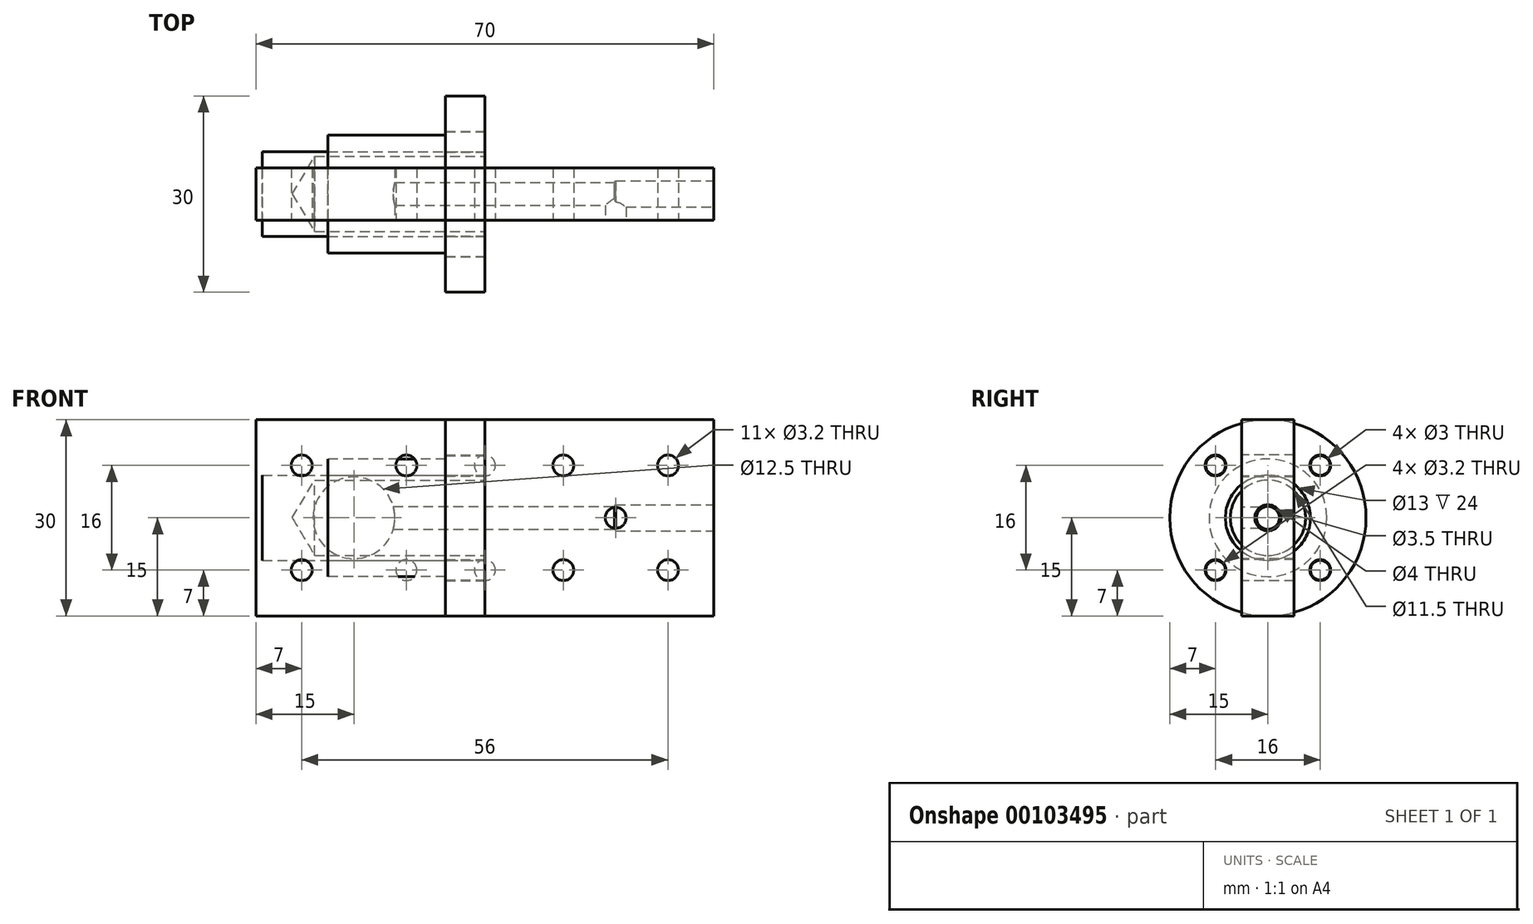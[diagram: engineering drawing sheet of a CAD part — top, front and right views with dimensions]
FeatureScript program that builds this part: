
annotation { "Feature Type Name" : "Feature", "Feature Type Description" : "" }
export const myFeature = defineFeature(function(context is Context, id is Id, definition is map)
    precondition{}
    {
        {
            var Q0;
            Q0=qCreatedBy(makeId("Front.planeOp"),FACE);
            var sketch = newSketch(context, id + "F0", { "sketchPlane" : qUnion([Q0])});
            skLineSegment(sketch, "E0.bottom", {"start": v(35, -15) * mm, "end": v(-35, -15) * mm});
            skLineSegment(sketch, "E0.top", {"start": v(35, 15) * mm, "end": v(-35, 15) * mm});
            skLineSegment(sketch, "E0.left", {"start": v(35, -15) * mm, "end": v(35, 15) * mm});
            skLineSegment(sketch, "E0.right", {"start": v(-35, -15) * mm, "end": v(-35, 15) * mm});
            skPoint(sketch, "E0.middle", {"position": v(0, 0) * mm});
            skSolve(sketch);
        }
        {
            var Q0;
            Q0=makeQuery(id+"F0.imprint","IMPRINT",FACE,{"disambiguationData":[TD([[makeQuery(id+"F0.imprint","IMPRINT",EDGE,{"derivedFrom":sQuery(id+"F0.wireOp",EDGE,"E0.bottom")}),-1.0]])]});
            extrude(context, id + "F1", {"entities" : qUnion([Q0]), "endBound" : BoundingType.SYMMETRIC, "depth" : 8 * mm});
        }
        {
            var Q0;
            Q0=makeQuery(id+"F1.opExtrude","CAP_FACE",FACE,{"disambiguationData":[OSD([sQuery(id+"F0.wireOp",EDGE,"E0.bottom"),sQuery(id+"F0.wireOp",EDGE,"E0.top"),sQuery(id+"F0.wireOp",EDGE,"E0.left"),sQuery(id+"F0.wireOp",EDGE,"E0.right")])],"isStart":false});
            var sketch = newSketch(context, id + "F2", { "sketchPlane" : qUnion([Q0])});
            skCircle(sketch, "E1", {"center": v(-20, 0) * mm, "radius": 6.25 * mm});
            skCircle(sketch, "E2", {"center": v(-28, 8) * mm, "radius": 1.6 * mm});
            skCircle(sketch, "E3", {"center": v(-12, 8) * mm, "radius": 1.6 * mm});
            skCircle(sketch, "E4", {"center": v(12, 8) * mm, "radius": 1.6 * mm});
            skCircle(sketch, "E5", {"center": v(28, 8) * mm, "radius": 1.6 * mm});
            skCircle(sketch, "E6", {"center": v(28, -8) * mm, "radius": 1.6 * mm});
            skCircle(sketch, "E7", {"center": v(12, -8) * mm, "radius": 1.6 * mm});
            skCircle(sketch, "E8", {"center": v(-12, -8) * mm, "radius": 1.6 * mm});
            skCircle(sketch, "E9", {"center": v(-28, -8) * mm, "radius": 1.6 * mm});
            skCircle(sketch, "E10", {"center": v(0, 8) * mm, "radius": 1.6 * mm});
            skCircle(sketch, "E11", {"center": v(0, -8) * mm, "radius": 1.6 * mm});
            skSolve(sketch);
        }
        {
            var Q0;
            Q0 = qSketchRegion(id + "F2", true);
            extrude(context, id + "F3", {"entities" : qUnion([Q0]), "operationType" : NewBodyOperationType.REMOVE, "endBound" : BoundingType.THROUGH_ALL, "oppositeDirection" : true, "depth" : 25 * mm});
        }
        {
            var Q0;
            Q0=makeQuery(id+"F1.opExtrude","CAP_FACE",FACE,{"disambiguationData":[OSD([sQuery(id+"F0.wireOp",EDGE,"E0.bottom"),sQuery(id+"F0.wireOp",EDGE,"E0.top"),sQuery(id+"F0.wireOp",EDGE,"E0.left"),sQuery(id+"F0.wireOp",EDGE,"E0.right")])],"isStart":false});
            var sketch = newSketch(context, id + "F4", { "sketchPlane" : qUnion([Q0])});
            skCircle(sketch, "E12", {"center": v(20, 0) * mm, "radius": 1.6 * mm});
            skPoint(sketch, "E12.centerSnap0", {"position": v(35, 0) * mm});
            skSolve(sketch);
        }
        {
            var Q0;
            Q0 = qSketchRegion(id + "F4", true);
            extrude(context, id + "F5", {"entities" : qUnion([Q0]), "operationType" : NewBodyOperationType.REMOVE, "oppositeDirection" : true, "depth" : 4 * mm});
        }
        {
            var Q0;
            Q0=makeQuery(id+"F1.opExtrude","SWEPT_FACE",FACE,{"disambiguationData":[OSD([sQuery(id+"F0.wireOp",EDGE,"E0.left")])]});
            var sketch = newSketch(context, id + "F6", { "sketchPlane" : qUnion([Q0])});
            skCircle(sketch, "E13", {"center": v(0, 0) * mm, "radius": 1.75 * mm});
            skSolve(sketch);
        }
        {
            var Q0;
            Q0 = qSketchRegion(id + "F6", true);
            var Q1;
            Q1=makeQuery(id+"F3.boolean.opBoolean","COPY",FACE,{"derivedFrom":makeQuery(id+"F3.opExtrude","SWEPT_FACE",FACE,{"disambiguationData":[OSD([sQuery(id+"F2.wireOp",EDGE,"E1")])]})});
            extrude(context, id + "F7", {"entities" : qUnion([Q0]), "operationType" : NewBodyOperationType.REMOVE, "endBound" : BoundingType.UP_TO_SURFACE, "oppositeDirection" : true, "endBoundEntityFace" : qUnion([Q1]), "depth" : 50 * mm});
        }
        {
            var Q0;
            Q0=makeQuery(id+"F1.opExtrude","SWEPT_FACE",FACE,{"disambiguationData":[OSD([sQuery(id+"F0.wireOp",EDGE,"E0.left")])]});
            var sketch = newSketch(context, id + "F8", { "sketchPlane" : qUnion([Q0])});
            skCircle(sketch, "E14", {"center": v(0, 0) * mm, "radius": 2 * mm});
            skSolve(sketch);
        }
        {
            var Q0;
            Q0=qCreatedBy(makeId("Front.planeOp"),FACE);
            var sketch = newSketch(context, id + "F9", { "sketchPlane" : qUnion([Q0])});
            skLineSegment(sketch, "E15", {"start": v(-24, 0) * mm, "end": v(-24, 9) * mm});
            skLineSegment(sketch, "E16", {"start": v(-24, 9) * mm, "end": v(-6, 9) * mm});
            skLineSegment(sketch, "E17", {"start": v(-6, 9) * mm, "end": v(-6, 15) * mm});
            skLineSegment(sketch, "E18", {"start": v(-6, 15) * mm, "end": v(0, 15) * mm});
            skLineSegment(sketch, "E19", {"start": v(0, 15) * mm, "end": v(0, 0) * mm});
            skLineSegment(sketch, "E20", {"start": v(-24, 0) * mm, "end": v(0, 0) * mm});
            skSolve(sketch);
        }
        {
            var Q0;
            Q0=makeQuery(id+"F9.imprint","IMPRINT",FACE,{"disambiguationData":[TD([[makeQuery(id+"F9.imprint","IMPRINT",EDGE,{"derivedFrom":sQuery(id+"F9.wireOp",EDGE,"E15")}),-1.0]])]});
            var Q1;
            Q1=sQuery(id+"F9.wireOp",EDGE,"E20");
            revolve(context, id + "F10", {"entities" : qUnion([Q0]), "axis" : qUnion([Q1]), "revolveType" : RevolveType.FULL});
        }
        {
            var Q0;
            Q0=makeQuery(id+"F10.opRevolve","SWEPT_FACE",FACE,{"disambiguationData":[OSD([sQuery(id+"F9.wireOp",EDGE,"E19")])]});
            var sketch = newSketch(context, id + "F11", { "sketchPlane" : qUnion([Q0])});
            skPoint(sketch, "E21", {"position": v(0, 0) * mm});
            skPoint(sketch, "E22", {"position": v(-8, 8) * mm});
            skPoint(sketch, "E23.MirrorP", {"position": v(8, 8) * mm});
            skPoint(sketch, "E24.MirrorP", {"position": v(-8, -8) * mm});
            skPoint(sketch, "E25.MirrorP", {"position": v(8, -8) * mm});
            skSolve(sketch);
        }
        {
            var Q0;
            Q0=sQuery(id+"F11.wireOp",VERTEX,"E22");
            var Q1;
            Q1=sQuery(id+"F11.wireOp",VERTEX,"E23.MirrorP");
            var Q2;
            Q2=sQuery(id+"F11.wireOp",VERTEX,"E25.MirrorP");
            var Q3;
            Q3=sQuery(id+"F11.wireOp",VERTEX,"E24.MirrorP");
            var Q4;
            Q4=makeQuery(id+"F10.opRevolve","SWEPT_BODY",BODY,{"disambiguationData":[OSD([sQuery(id+"F9.wireOp",EDGE,"E15"),sQuery(id+"F9.wireOp",EDGE,"E16"),sQuery(id+"F9.wireOp",EDGE,"E17"),sQuery(id+"F9.wireOp",EDGE,"E18"),sQuery(id+"F9.wireOp",EDGE,"E19"),sQuery(id+"F9.wireOp",EDGE,"E20")])]});
            hole(context, id + "F12", {"style" : HoleStyle.SIMPLE, "endStyle" : HoleEndStyle.THROUGH, "holeDiameter" : 3 * mm, "locations" : qUnion([Q0, Q1, Q2, Q3]), "scope" : qUnion([Q4]), "isTappedThrough" : true});
        }
        {
            var Q0;
            Q0=sQuery(id+"F11.wireOp",VERTEX,"E21");
            var Q1;
            Q1=makeQuery(id+"F10.opRevolve","SWEPT_BODY",BODY,{"disambiguationData":[OSD([sQuery(id+"F9.wireOp",EDGE,"E15"),sQuery(id+"F9.wireOp",EDGE,"E16"),sQuery(id+"F9.wireOp",EDGE,"E17"),sQuery(id+"F9.wireOp",EDGE,"E18"),sQuery(id+"F9.wireOp",EDGE,"E19"),sQuery(id+"F9.wireOp",EDGE,"E20")])]});
            hole(context, id + "F13", {"style" : HoleStyle.SIMPLE, "endStyle" : HoleEndStyle.THROUGH, "holeDiameter" : 13 * mm, "locations" : qUnion([Q0]), "scope" : qUnion([Q1]), "isTappedThrough" : true});
        }
        {
            var Q0;
            Q0=sQuery(id+"F8.wireOp",VERTEX,"E14.center");
            var Q1;
            Q1=makeQuery(id+"F1.opExtrude","SWEPT_BODY",BODY,{"disambiguationData":[OSD([sQuery(id+"F0.wireOp",EDGE,"E0.bottom"),sQuery(id+"F0.wireOp",EDGE,"E0.top"),sQuery(id+"F0.wireOp",EDGE,"E0.left"),sQuery(id+"F0.wireOp",EDGE,"E0.right")])]});
            hole(context, id + "F14", {"style" : HoleStyle.SIMPLE, "endStyle" : HoleEndStyle.BLIND, "holeDiameter" : 4 * mm, "holeDepth" : 15 * mm, "locations" : qUnion([Q0]), "scope" : qUnion([Q1])});
        }
        {
            var Q0;
            Q0=qCreatedBy(makeId("Front.planeOp"),FACE);
            var sketch = newSketch(context, id + "F15", { "sketchPlane" : qUnion([Q0])});
            skLineSegment(sketch, "E26", {"start": v(0, 0) * mm, "end": v(-34, 0) * mm});
            skLineSegment(sketch, "E27", {"start": v(-34, 0) * mm, "end": v(-34, 6.5) * mm});
            skLineSegment(sketch, "E28", {"start": v(-34, 6.5) * mm, "end": v(-6, 6.5) * mm});
            skLineSegment(sketch, "E29", {"start": v(-6, 6.5) * mm, "end": v(-6, 15) * mm});
            skLineSegment(sketch, "E30", {"start": v(-6, 15) * mm, "end": v(0, 15) * mm});
            skLineSegment(sketch, "E31", {"start": v(0, 15) * mm, "end": v(0, 0) * mm});
            skSolve(sketch);
        }
        {
            var Q0;
            Q0=makeQuery(id+"F15.imprint","IMPRINT",FACE,{"disambiguationData":[TD([[makeQuery(id+"F15.imprint","IMPRINT",EDGE,{"derivedFrom":sQuery(id+"F15.wireOp",EDGE,"E26")}),-1.0]])]});
            var Q1;
            Q1=sQuery(id+"F15.wireOp",EDGE,"E26");
            revolve(context, id + "F16", {"entities" : qUnion([Q0]), "axis" : qUnion([Q1]), "revolveType" : RevolveType.FULL});
        }
        {
            var Q0;
            Q0=sQuery(id+"F11.wireOp",VERTEX,"E22");
            var Q1;
            Q1=sQuery(id+"F11.wireOp",VERTEX,"E23.MirrorP");
            var Q2;
            Q2=sQuery(id+"F11.wireOp",VERTEX,"E25.MirrorP");
            var Q3;
            Q3=sQuery(id+"F11.wireOp",VERTEX,"E24.MirrorP");
            var Q4;
            Q4=makeQuery(id+"F16.opRevolve","SWEPT_BODY",BODY,{"disambiguationData":[OSD([sQuery(id+"F15.wireOp",EDGE,"E26"),sQuery(id+"F15.wireOp",EDGE,"E27"),sQuery(id+"F15.wireOp",EDGE,"E28"),sQuery(id+"F15.wireOp",EDGE,"E29"),sQuery(id+"F15.wireOp",EDGE,"E30"),sQuery(id+"F15.wireOp",EDGE,"E31")])]});
            hole(context, id + "F17", {"style" : HoleStyle.SIMPLE, "endStyle" : HoleEndStyle.THROUGH, "holeDiameter" : 3.2 * mm, "locations" : qUnion([Q0, Q1, Q2, Q3]), "scope" : qUnion([Q4]), "isTappedThrough" : true});
        }
        {
            var Q0;
            Q0=sQuery(id+"F11.wireOp",VERTEX,"E21");
            var Q1;
            Q1=makeQuery(id+"F16.opRevolve","SWEPT_BODY",BODY,{"disambiguationData":[OSD([sQuery(id+"F15.wireOp",EDGE,"E26"),sQuery(id+"F15.wireOp",EDGE,"E27"),sQuery(id+"F15.wireOp",EDGE,"E28"),sQuery(id+"F15.wireOp",EDGE,"E29"),sQuery(id+"F15.wireOp",EDGE,"E30"),sQuery(id+"F15.wireOp",EDGE,"E31")])]});
            hole(context, id + "F18", {"style" : HoleStyle.SIMPLE, "endStyle" : HoleEndStyle.BLIND, "holeDiameter" : 11.5 * mm, "holeDepth" : 26 * mm, "locations" : qUnion([Q0]), "scope" : qUnion([Q1])});
        }
    });
